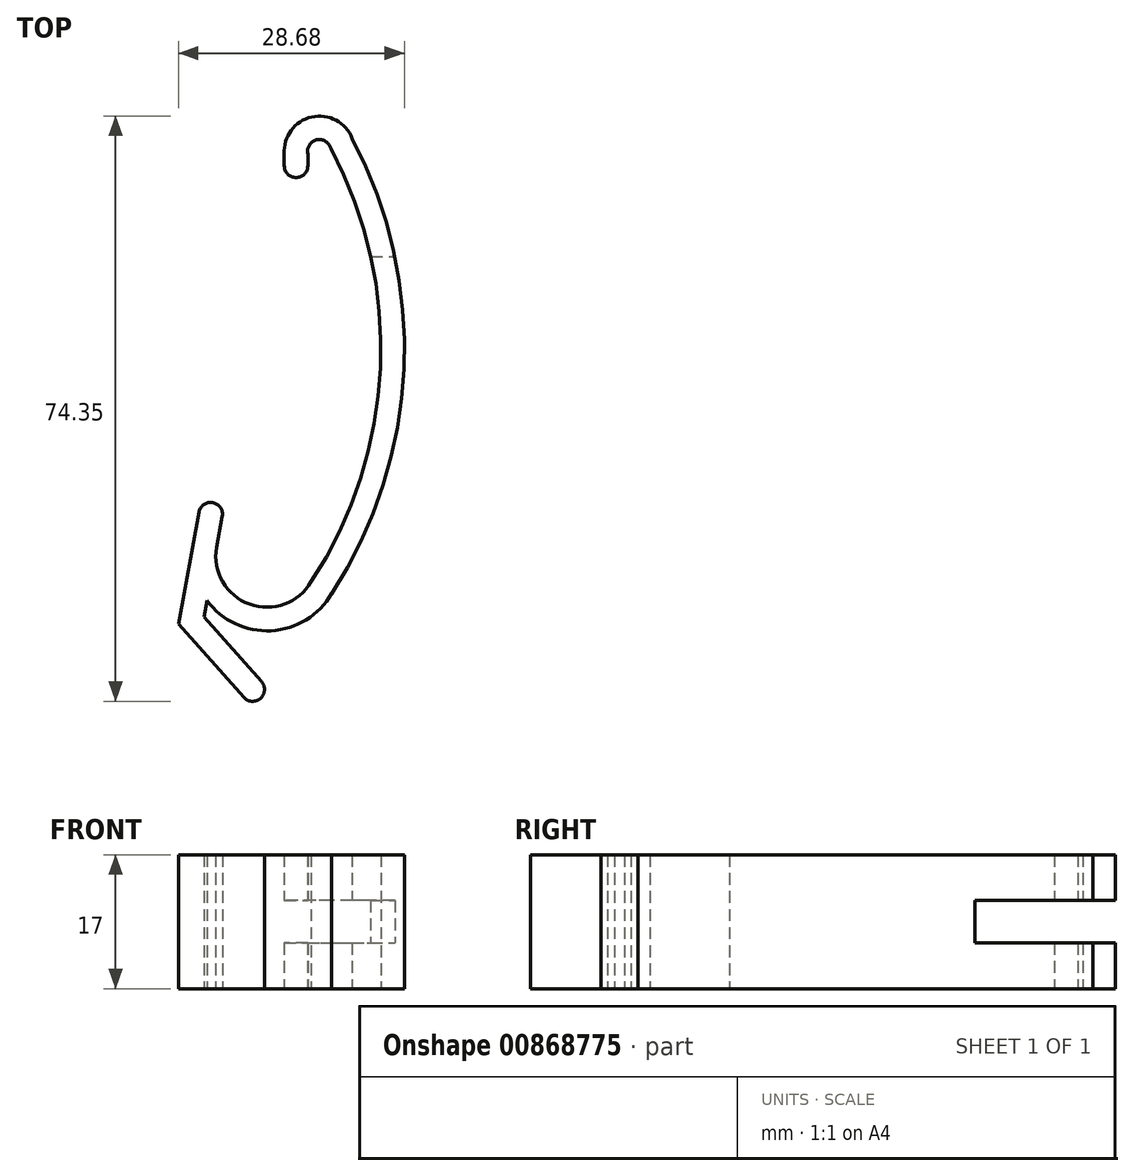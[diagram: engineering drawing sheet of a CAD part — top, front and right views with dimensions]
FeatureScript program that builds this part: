
annotation { "Feature Type Name" : "Feature", "Feature Type Description" : "" }
export const myFeature = defineFeature(function(context is Context, id is Id, definition is map)
    precondition{}
    {
        {
            var Q0;
            Q0=qCreatedBy(makeId("Top.planeOp"),FACE);
            var sketch = newSketch(context, id + "F0", { "sketchPlane" : qUnion([Q0])});
            skArc(sketch, "E0", {"start": v(5.6, 28.16) * mm, "mid": v(3.8, 29.3) * mm, "end": v(2.66, 27.5) * mm});
            skLineSegment(sketch, "E1", {"start": v(2.66, 27.5) * mm, "end": v(2.66, 26) * mm});
            skArc(sketch, "E2", {"start": v(-8.93, -22.47) * mm, "mid": v(-4.74, -29.7) * mm, "end": v(3.1, -26.84) * mm});
            skArc(sketch, "E3", {"start": v(3.1, -26.84) * mm, "mid": v(11.87, 0.32) * mm, "end": v(5.6, 28.16) * mm});
            skLineSegment(sketch, "E4", {"start": v(-8.93, -22.47) * mm, "end": v(-10.55, -31.33) * mm});
            skLineSegment(sketch, "E5", {"start": v(-10.55, -31.33) * mm, "end": v(-3.23, -39.54) * mm});
            skLineSegment(sketch, "E6", {"start": v(-8.93, -22.47) * mm, "end": v(-8.21, -18.54) * mm});
            skLineSegment(sketch, "E7", {"start": v(2.66, 26) * mm, "end": v(-0.34, 26) * mm, "construction": true});
            skLineSegment(sketch, "E8", {"start": v(-0.34, 26) * mm, "end": v(-0.34, 27.5) * mm});
            skLineSegment(sketch, "E9", {"start": v(5.6, 28.16) * mm, "end": v(8.3, 29.45) * mm, "construction": true});
            skArc(sketch, "E10", {"start": v(8.3, 29.45) * mm, "mid": v(3.14, 32.2) * mm, "end": v(-0.34, 27.5) * mm});
            skLineSegment(sketch, "E11", {"start": v(2.18, 31.86) * mm, "end": v(3.68, 29.26) * mm, "construction": true});
            skLineSegment(sketch, "E12", {"start": v(3.1, -26.84) * mm, "end": v(5.68, -28.37) * mm, "construction": true});
            skLineSegment(sketch, "E13", {"start": v(-8.21, -18.54) * mm, "end": v(-11.16, -18) * mm, "construction": true});
            skLineSegment(sketch, "E14", {"start": v(-8.93, -22.47) * mm, "end": v(-11.88, -21.94) * mm});
            skLineSegment(sketch, "E15", {"start": v(-11.16, -18) * mm, "end": v(-11.88, -21.94) * mm});
            skArc(sketch, "E16", {"start": v(-11.88, -21.94) * mm, "mid": v(-5.8, -32.5) * mm, "end": v(5.68, -28.37) * mm});
            skArc(sketch, "E17", {"start": v(5.68, -28.37) * mm, "mid": v(14.86, 0.18) * mm, "end": v(8.3, 29.45) * mm});
            skLineSegment(sketch, "E18", {"start": v(11.87, 0.32) * mm, "end": v(14.87, 0.32) * mm, "construction": true});
            skLineSegment(sketch, "E19", {"start": v(-5.88, -29.15) * mm, "end": v(-7.4, -31.73) * mm});
            skLineSegment(sketch, "E20", {"start": v(-3.23, -39.54) * mm, "end": v(-5.47, -41.53) * mm, "construction": true});
            skLineSegment(sketch, "E21", {"start": v(-5.47, -41.53) * mm, "end": v(-13.76, -32.23) * mm});
            skLineSegment(sketch, "E22", {"start": v(-13.76, -32.23) * mm, "end": v(-12.34, -24.44) * mm});
            skLineSegment(sketch, "E23", {"start": v(-12.34, -24.44) * mm, "end": v(-11.88, -21.94) * mm});
            skArc(sketch, "E24", {"start": v(-8.21, -18.54) * mm, "mid": v(-9.42, -16.8) * mm, "end": v(-11.16, -18) * mm});
            skArc(sketch, "E25", {"start": v(-5.47, -41.53) * mm, "mid": v(-3.35, -41.66) * mm, "end": v(-3.23, -39.54) * mm});
            skArc(sketch, "E26", {"start": v(-0.34, 26) * mm, "mid": v(1.16, 24.5) * mm, "end": v(2.66, 26) * mm});
            skSolve(sketch);
        }
        {
            var Q0;
            Q0=makeQuery(id+"F0.imprint","IMPRINT",FACE,{"disambiguationData":[TD([[makeQuery(id+"F0.imprint","IMPRINT",EDGE,{"derivedFrom":sQuery(id+"F0.wireOp",EDGE,"E6")}),1.0]])]});
            var Q1;
            Q1=makeQuery(id+"F0.imprint","IMPRINT",FACE,{"disambiguationData":[TD([[makeQuery(id+"F0.imprint","IMPRINT",EDGE,{"derivedFrom":sQuery(id+"F0.wireOp",EDGE,"E0")}),-1.0]])]});
            var Q2;
            {var subQ4=sQuery(id+"F0.wireOp",EDGE,"E5");Q2=makeQuery(id+"F0.imprint","IMPRINT",FACE,{"disambiguationData":[TD([[makeQuery(id+"F0.imprint","IMPRINT",EDGE,{"derivedFrom":subQ4}),-1.0]])]});}
            var Q3;
            {var subQ3=sQuery(id+"F0.wireOp",EDGE,"E19");Q3=makeQuery(id+"F0.imprint","IMPRINT",FACE,{"disambiguationData":[TD([[makeQuery(id+"F0.imprint","IMPRINT",EDGE,{"derivedFrom":subQ3}),-1.0]])]});}
            var Q4;
            {var subQ0=sQuery(id+"F0.wireOp",EDGE,"E14");Q4=makeQuery(id+"F0.imprint","IMPRINT",FACE,{"disambiguationData":[TD([[makeQuery(id+"F0.imprint","IMPRINT",EDGE,{"derivedFrom":subQ0}),1.0]])]});}
            extrude(context, id + "F1", {"entities" : qUnion([Q0, Q1, Q2, Q3, Q4]), "depth" : 17 * mm, "offsetDistance" : 25 * mm});
        }
        {
            var Q0;
            Q0=qCreatedBy(makeId("Right.planeOp"),FACE);
            var sketch = newSketch(context, id + "F2", { "sketchPlane" : qUnion([Q0])});
            skLineSegment(sketch, "E27", {"start": v(28.45, 11.2) * mm, "end": v(14.45, 11.2) * mm});
            skLineSegment(sketch, "E28", {"start": v(14.45, 11.2) * mm, "end": v(14.45, 5.8) * mm});
            skLineSegment(sketch, "E29", {"start": v(14.45, 5.8) * mm, "end": v(49.33, 5.8) * mm});
            skLineSegment(sketch, "E30", {"start": v(49.33, 5.8) * mm, "end": v(49.33, 11.2) * mm});
            skLineSegment(sketch, "E31", {"start": v(49.33, 11.2) * mm, "end": v(28.45, 11.2) * mm});
            skSolve(sketch);
        }
        {
            var Q0;
            Q0=makeQuery(id+"F2.imprint","IMPRINT",FACE,{"disambiguationData":[TD([[makeQuery(id+"F2.imprint","IMPRINT",EDGE,{"derivedFrom":sQuery(id+"F2.wireOp",EDGE,"E27")}),1.0]])]});
            extrude(context, id + "F3", {"entities" : qUnion([Q0]), "operationType" : NewBodyOperationType.REMOVE, "oppositeDirection" : true, "depth" : 150 * mm, "offsetDistance" : 25 * mm, "hasSecondDirection" : true, "secondDirectionOppositeDirection" : false, "secondDirectionDepth" : 25 * mm});
        }
    });
